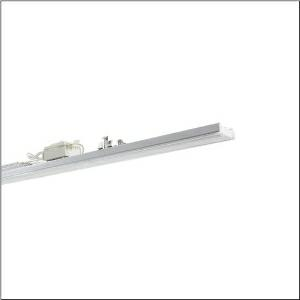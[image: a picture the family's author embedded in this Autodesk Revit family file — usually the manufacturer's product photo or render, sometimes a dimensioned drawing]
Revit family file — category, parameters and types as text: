
# Revit family: licross_r__21_recessed_mo_52tl18vn455g_e944
name_source: partatom
category: Lighting Fixtures
units: mm (PartAtom-declared; Revit-internal decimal feet)

## family parameters
Cut with Voids When Loaded = No
Host = Face
Light Source = No
Part Type = Normal
Room Calculation Point = No
Round Connector Dimension = Use Diameter
Shared = No

## types (1)
- --- (1 x LED, 5500 lm, 30.5 W, 4000K)
    Apparent Load = 31 VA
    CIE Flux Codes = 79 95 99 100 100
    Color Rendering = 80
    Color Temperature = 4000K
    Default Elevation = 1800 mm
    Description = Licross® 21 Recessed MO, luminaire insert, of sheet steel, galvanised, coil coated, white, length: 1.500mm, width: 66mm, height: 67mm, LED rated luminous flux: 5.500lm, light colour: 840, control gear: DALI 2, CLO, with plug, 5-pole, with phase selection, mains connection: 220..240V, AC, 50/60Hz, start of lifetime: 31W, end of service life: 36W, halogen-free wiring, primary optical cover: cover, of PMMA, light emission: direct distribution, primary light characteristic: symmetric, protection rating (complete): IP40, insulation class (complete): insulation class I (protective earthing), certification: CE, ENEC, VDE, UKCA, protection symbol: D if used in an environment without relevant dust loads with corresponding accessories, impact resistance: IK06, permissible ambient temperature for indoor applications: -25..+45°C, corresponds to IFS (International Featured Standards) requirements for safety and quality in the food industry, reducing of maximum allowable ambient temperature of 5°C with ceiling mounting, LABS conformity tested according to VDMA 24364:2018-05, packaging unit: 1 piece
    Height = 58 mm
    Lamp = 1 x LED
    Lamp Light Flux = 5500 lm
    Lamp Power = 30.5 W
    Lamp count = 1
    Length = 1500 mm
    Luminous efficacy = 180 lm/W
    Manufacturer = Siteco
    ModVariant = No
    Model = 52TL18VN455G
    Mounting Place = Ceiling
    Mounting Type = Pendant
    Number of Poles = 1
    OnlyDefault = Yes
    Power Factor = 1
    Product Name = Licross® 21 Recessed MO
    Product group = luminaire insert
    ProductGroupID = 902
    Protection Class = Protection class I
    Protection Degree = IP 40
    RLX_Detail_Level = 1
    RLX_Emergency_Light_Flux = 0 lm
    RLX_Emergency_Type = 0
    RLX_Emergency_Type_DB = No
    RlxData = <blob elided: 23921 chars, md5=afdd131c>
    Socket = socket
    Standby Power = 0 W
    System Light Flux = 5500 lm
    System Power = 31 W
    Type Comments = factory setting: luminous flux: 100 % | dim-lin: 254 | 206 mA
    Type Image = l_1296930.jpg
    URL = http://relux.com
    VarID = @adj_082200
    Voltage = 0 V
    Weight = 0.00 kg
    Width = 66 mm

## geometry (parser evidence)
native form markers: Blend x4, Sweep x9
no freeform markers — native parametric forms only
